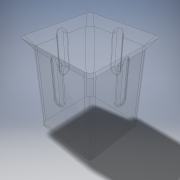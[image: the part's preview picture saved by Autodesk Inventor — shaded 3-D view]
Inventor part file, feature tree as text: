
AUTODESK INVENTOR PART (.ipt)
format: ipt  version: 2017 (Build 210142000, 142)  size: 330,752 bytes
history: native  units: mm
features: extrude x8, sketch x8, fillet x3, projected_geometry x3, chamfer x1
ambient origin geometry x8: Origin, YZ Plane, XZ Plane, XY Plane, X Axis, Y Axis, Z Axis, Center Point
bodies: Volumenkörper1 (feature_tree)
feature tree (23):
  extrude  "Extrusion1"  Depth=2.9mm
  extrude  "Extrusion2"  Depth=4.0mm
  extrude  "Extrusion3"  Depth=0.4mm TaperAngle=0.0deg
  extrude  "Extrusion4"  Depth=0.4mm TaperAngle=0.0deg
  chamfer  "Fase1"  Distance=0.5mm Angle=45.0deg
  extrude  "Extrusion5"  Depth=1.45mm
  extrude  "Extrusion6"  Depth=0.15mm TaperAngle=0.0deg
  extrude  "Extrusion7"  Depth=1.5mm
  extrude  "Extrusion8"  Depth=0.25mm TaperAngle=0.0deg
  fillet  "Rundung1"  Radius=0.1mm
  fillet  "Rundung2"  Radius=0.25mm
  fillet  "Rundung3"  Radius=0.25mm
  sketch  "Skizze1"  dims[d0=2.9mm d1=2.9mm]
  sketch  "Skizze2"  dims[d2=4.0mm d3=0.0mm d4=3.4mm]
  sketch  "Skizze3"  dims[d5=3.4mm d6=0.4mm d7=0.0mm]
  sketch  "Skizze4"  dims[d8=0.4mm d9=0.0mm d10=0.4mm d11=0.0mm d12=0.5mm d13=2.0mm d14=45.0deg]
  sketch  "Skizze5"  dims[d15=1.45mm d16=1.5mm]
  projected_geometry  "Projizierte Kontur1"
  sketch  "Skizze6"  dims[d17=0.5mm d18=0.15mm d19=0.0mm]
  projected_geometry  "Projizierte Kontur2"
  sketch  "Skizze7"  dims[d20=0.15mm d21=0.0mm d22=1.5mm d23=0.5mm]
  sketch  "Skizze8"  dims[d24=0.15mm d25=0.0mm d26=0.15mm d27=0.0mm d28=0.1mm d29=0.25mm d30=0.25mm]
  projected_geometry  "Projizierte Kontur3"
